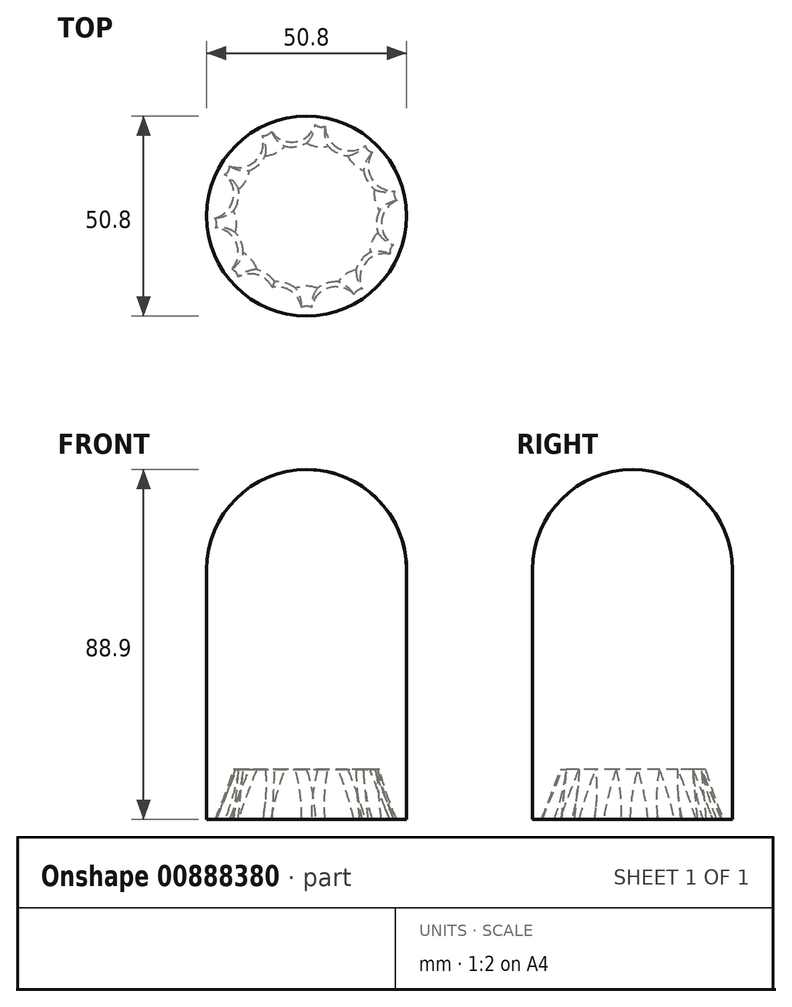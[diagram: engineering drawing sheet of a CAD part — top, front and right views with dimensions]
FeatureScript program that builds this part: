
annotation { "Feature Type Name" : "Feature", "Feature Type Description" : "" }
export const myFeature = defineFeature(function(context is Context, id is Id, definition is map)
    precondition{}
    {
        {
            var Q0;
            Q0=qCreatedBy(makeId("Front.planeOp"),FACE);
            var sketch = newSketch(context, id + "F0", { "sketchPlane" : qUnion([Q0])});
            skLineSegment(sketch, "E0.bottom", {"start": v(-25.4, 0) * mm, "end": v(25.4, 0) * mm});
            skLineSegment(sketch, "E0.top", {"start": v(-25.4, 50.8) * mm, "end": v(25.4, 50.8) * mm});
            skLineSegment(sketch, "E0.left", {"start": v(-25.4, 0) * mm, "end": v(-25.4, 50.8) * mm});
            skLineSegment(sketch, "E0.right", {"start": v(25.4, 0) * mm, "end": v(25.4, 50.8) * mm});
            skPoint(sketch, "E0.middle", {"position": v(0, 25.4) * mm});
            skArc(sketch, "E1", {"start": v(-25.4, 50.8) * mm, "mid": v(0, 76.2) * mm, "end": v(25.4, 50.8) * mm});
            skLineSegment(sketch, "E2", {"start": v(0, 0) * mm, "end": v(0, 76.2) * mm});
            skSolve(sketch);
        }
        {
            var Q0;
            {var subQ0=sQuery(id+"F0.wireOp",EDGE,"E1");var subQ3=sQuery(id+"F0.wireOp",EDGE,"E2");var subQ5=makeQuery(id+"F0.imprint","INTERSECT",VERTEX,{"derivedFrom":[subQ0,subQ3]});Q0=makeQuery(id+"F0.imprint","IMPRINT",FACE,{"disambiguationData":[TD([[makeQuery(id+"F0.imprint","IMPRINT",EDGE,{"disambiguationData":[TD([[subQ5,1.0]])],"derivedFrom":subQ3}),1.0]])]});}
            var Q1;
            {var subQ0=sQuery(id+"F0.wireOp",EDGE,"E0.left");Q1=makeQuery(id+"F0.imprint","IMPRINT",FACE,{"disambiguationData":[TD([[makeQuery(id+"F0.imprint","IMPRINT",EDGE,{"derivedFrom":subQ0}),-1.0]])]});}
            var Q2;
            Q2=sQuery(id+"F0.wireOp",EDGE,"E2");
            revolve(context, id + "F1", {"surfaceOperationType" : NewSurfaceOperationType.NEW, "entities" : qUnion([Q0, Q1]), "axis" : qUnion([Q2]), "revolveType" : RevolveType.FULL});
        }
        {
            var Q0;
            Q0=makeQuery(id+"F1.opRevolve","SWEPT_FACE",FACE,{"disambiguationData":[OSD([sQuery(id+"F0.wireOp",EDGE,"E0.bottom")])]});
            var sketch = newSketch(context, id + "F2", { "sketchPlane" : qUnion([Q0])});
            skCircle(sketch, "E3", {"center": v(0, 25.4) * mm, "radius": 7.57 * mm});
            skCircle(sketch, "E4", {"center": v(-7.49, 24.27) * mm, "radius": 7.57 * mm});
            skCircle(sketch, "E5", {"center": v(-14.3, 20.99) * mm, "radius": 7.57 * mm});
            skCircle(sketch, "E6", {"center": v(-19.86, 15.84) * mm, "radius": 7.57 * mm});
            skCircle(sketch, "E7", {"center": v(-23.64, 9.28) * mm, "radius": 7.57 * mm});
            skCircle(sketch, "E8", {"center": v(-25.33, 1.9) * mm, "radius": 7.57 * mm});
            skCircle(sketch, "E9", {"center": v(-24.76, -5.65) * mm, "radius": 7.57 * mm});
            skCircle(sketch, "E10", {"center": v(-22, -12.7) * mm, "radius": 7.57 * mm});
            skCircle(sketch, "E11", {"center": v(-17.28, -18.62) * mm, "radius": 7.57 * mm});
            skCircle(sketch, "E12", {"center": v(-11.02, -22.88) * mm, "radius": 7.57 * mm});
            skCircle(sketch, "E13", {"center": v(-3.79, -25.12) * mm, "radius": 7.57 * mm});
            skCircle(sketch, "E14", {"center": v(3.79, -25.12) * mm, "radius": 7.57 * mm});
            skCircle(sketch, "E15", {"center": v(11.02, -22.88) * mm, "radius": 7.57 * mm});
            skCircle(sketch, "E16", {"center": v(17.28, -18.62) * mm, "radius": 7.57 * mm});
            skCircle(sketch, "E17", {"center": v(22, -12.7) * mm, "radius": 7.57 * mm});
            skCircle(sketch, "E18", {"center": v(24.76, -5.65) * mm, "radius": 7.57 * mm});
            skCircle(sketch, "E19", {"center": v(25.33, 1.9) * mm, "radius": 7.57 * mm});
            skCircle(sketch, "E20", {"center": v(23.64, 9.28) * mm, "radius": 7.57 * mm});
            skCircle(sketch, "E21", {"center": v(19.86, 15.84) * mm, "radius": 7.57 * mm});
            skCircle(sketch, "E22", {"center": v(14.3, 20.99) * mm, "radius": 7.57 * mm});
            skCircle(sketch, "E23", {"center": v(7.49, 24.27) * mm, "radius": 7.57 * mm});
            skSolve(sketch);
        }
        {
            var Q0;
            Q0 = qSketchRegion(id + "F2", true);
            var Q1;
            {var subQ0=sQuery(id+"F2.wireOp",EDGE,"E12");var subQ1=sQuery(id+"F2.wireOp",EDGE,"E10");var subQ2=makeQuery(id+"F2.imprint","INTERSECT",VERTEX,{"derivedFrom":[subQ1,subQ0]});Q1=makeQuery(id+"F2.imprint","IMPRINT",FACE,{"disambiguationData":[TD([[makeQuery(id+"F2.imprint","IMPRINT",EDGE,{"disambiguationData":[TD([[subQ2,1.0]])],"derivedFrom":subQ1}),1.0]])]});}
            var Q2;
            {var subQ0=sQuery(id+"F2.wireOp",EDGE,"E12");var subQ1=sQuery(id+"F2.wireOp",EDGE,"E11");var subQ2=makeQuery(id+"F2.imprint","INTERSECT",VERTEX,{"disambiguationData":[OD(1.0)],"derivedFrom":[subQ1,subQ0]});Q2=makeQuery(id+"F2.imprint","IMPRINT",FACE,{"disambiguationData":[TD([[makeQuery(id+"F2.imprint","IMPRINT",EDGE,{"disambiguationData":[TD([[subQ2,1.0]])],"derivedFrom":subQ1}),-1.0]])]});}
            var Q3;
            {var subQ0=sQuery(id+"F2.wireOp",EDGE,"E13");var subQ1=sQuery(id+"F2.wireOp",EDGE,"E11");var subQ2=makeQuery(id+"F2.imprint","INTERSECT",VERTEX,{"derivedFrom":[subQ1,subQ0]});Q3=makeQuery(id+"F2.imprint","IMPRINT",FACE,{"disambiguationData":[TD([[makeQuery(id+"F2.imprint","IMPRINT",EDGE,{"disambiguationData":[TD([[subQ2,1.0]])],"derivedFrom":subQ1}),1.0]])]});}
            var Q4;
            {var subQ0=sQuery(id+"F2.wireOp",EDGE,"E13");var subQ1=sQuery(id+"F2.wireOp",EDGE,"E12");var subQ2=makeQuery(id+"F2.imprint","INTERSECT",VERTEX,{"disambiguationData":[OD(1.0)],"derivedFrom":[subQ1,subQ0]});Q4=makeQuery(id+"F2.imprint","IMPRINT",FACE,{"disambiguationData":[TD([[makeQuery(id+"F2.imprint","IMPRINT",EDGE,{"disambiguationData":[TD([[subQ2,1.0]])],"derivedFrom":subQ1}),-1.0]])]});}
            var Q5;
            {var subQ0=sQuery(id+"F2.wireOp",EDGE,"E15");var subQ1=sQuery(id+"F2.wireOp",EDGE,"E13");var subQ2=makeQuery(id+"F2.imprint","INTERSECT",VERTEX,{"derivedFrom":[subQ1,subQ0]});Q5=makeQuery(id+"F2.imprint","IMPRINT",FACE,{"disambiguationData":[TD([[makeQuery(id+"F2.imprint","IMPRINT",EDGE,{"disambiguationData":[TD([[subQ2,-1.0]])],"derivedFrom":subQ1}),-1.0]])]});}
            var Q6;
            {var subQ0=sQuery(id+"F2.wireOp",EDGE,"E14");var subQ1=sQuery(id+"F2.wireOp",EDGE,"E12");var subQ2=makeQuery(id+"F2.imprint","INTERSECT",VERTEX,{"derivedFrom":[subQ1,subQ0]});Q6=makeQuery(id+"F2.imprint","IMPRINT",FACE,{"disambiguationData":[TD([[makeQuery(id+"F2.imprint","IMPRINT",EDGE,{"disambiguationData":[TD([[subQ2,1.0]])],"derivedFrom":subQ1}),1.0]])]});}
            var Q7;
            {var subQ0=sQuery(id+"F2.wireOp",EDGE,"E15");var subQ1=sQuery(id+"F2.wireOp",EDGE,"E13");var subQ2=makeQuery(id+"F2.imprint","INTERSECT",VERTEX,{"derivedFrom":[subQ1,subQ0]});Q7=makeQuery(id+"F2.imprint","IMPRINT",FACE,{"disambiguationData":[TD([[makeQuery(id+"F2.imprint","IMPRINT",EDGE,{"disambiguationData":[TD([[subQ2,1.0]])],"derivedFrom":subQ1}),1.0]])]});}
            var Q8;
            {var subQ0=sQuery(id+"F2.wireOp",EDGE,"E16");var subQ1=sQuery(id+"F2.wireOp",EDGE,"E14");var subQ2=makeQuery(id+"F2.imprint","INTERSECT",VERTEX,{"derivedFrom":[subQ1,subQ0]});Q8=makeQuery(id+"F2.imprint","IMPRINT",FACE,{"disambiguationData":[TD([[makeQuery(id+"F2.imprint","IMPRINT",EDGE,{"disambiguationData":[TD([[subQ2,-1.0]])],"derivedFrom":subQ1}),-1.0]])]});}
            var Q9;
            {var subQ0=sQuery(id+"F2.wireOp",EDGE,"E17");var subQ1=sQuery(id+"F2.wireOp",EDGE,"E15");var subQ2=makeQuery(id+"F2.imprint","INTERSECT",VERTEX,{"derivedFrom":[subQ1,subQ0]});Q9=makeQuery(id+"F2.imprint","IMPRINT",FACE,{"disambiguationData":[TD([[makeQuery(id+"F2.imprint","IMPRINT",EDGE,{"disambiguationData":[TD([[subQ2,-1.0]])],"derivedFrom":subQ1}),-1.0]])]});}
            var Q10;
            {var subQ0=sQuery(id+"F2.wireOp",EDGE,"E18");var subQ1=sQuery(id+"F2.wireOp",EDGE,"E16");var subQ2=makeQuery(id+"F2.imprint","INTERSECT",VERTEX,{"derivedFrom":[subQ1,subQ0]});Q10=makeQuery(id+"F2.imprint","IMPRINT",FACE,{"disambiguationData":[TD([[makeQuery(id+"F2.imprint","IMPRINT",EDGE,{"disambiguationData":[TD([[subQ2,-1.0]])],"derivedFrom":subQ1}),-1.0]])]});}
            var Q11;
            {var subQ0=sQuery(id+"F2.wireOp",EDGE,"E17");var subQ1=sQuery(id+"F2.wireOp",EDGE,"E15");var subQ2=makeQuery(id+"F2.imprint","INTERSECT",VERTEX,{"derivedFrom":[subQ1,subQ0]});Q11=makeQuery(id+"F2.imprint","IMPRINT",FACE,{"disambiguationData":[TD([[makeQuery(id+"F2.imprint","IMPRINT",EDGE,{"disambiguationData":[TD([[subQ2,1.0]])],"derivedFrom":subQ1}),1.0]])]});}
            var Q12;
            {var subQ0=sQuery(id+"F2.wireOp",EDGE,"E16");var subQ1=sQuery(id+"F2.wireOp",EDGE,"E14");var subQ2=makeQuery(id+"F2.imprint","INTERSECT",VERTEX,{"derivedFrom":[subQ1,subQ0]});Q12=makeQuery(id+"F2.imprint","IMPRINT",FACE,{"disambiguationData":[TD([[makeQuery(id+"F2.imprint","IMPRINT",EDGE,{"disambiguationData":[TD([[subQ2,1.0]])],"derivedFrom":subQ1}),1.0]])]});}
            var Q13;
            {var subQ0=sQuery(id+"F2.wireOp",EDGE,"E20");var subQ1=sQuery(id+"F2.wireOp",EDGE,"E18");var subQ2=makeQuery(id+"F2.imprint","INTERSECT",VERTEX,{"derivedFrom":[subQ1,subQ0]});Q13=makeQuery(id+"F2.imprint","IMPRINT",FACE,{"disambiguationData":[TD([[makeQuery(id+"F2.imprint","IMPRINT",EDGE,{"disambiguationData":[TD([[subQ2,-1.0]])],"derivedFrom":subQ1}),-1.0]])]});}
            var Q14;
            {var subQ0=sQuery(id+"F2.wireOp",EDGE,"E18");var subQ1=sQuery(id+"F2.wireOp",EDGE,"E16");var subQ2=makeQuery(id+"F2.imprint","INTERSECT",VERTEX,{"derivedFrom":[subQ1,subQ0]});Q14=makeQuery(id+"F2.imprint","IMPRINT",FACE,{"disambiguationData":[TD([[makeQuery(id+"F2.imprint","IMPRINT",EDGE,{"disambiguationData":[TD([[subQ2,1.0]])],"derivedFrom":subQ1}),1.0]])]});}
            var Q15;
            {var subQ0=sQuery(id+"F2.wireOp",EDGE,"E19");var subQ1=sQuery(id+"F2.wireOp",EDGE,"E17");var subQ2=makeQuery(id+"F2.imprint","INTERSECT",VERTEX,{"derivedFrom":[subQ1,subQ0]});Q15=makeQuery(id+"F2.imprint","IMPRINT",FACE,{"disambiguationData":[TD([[makeQuery(id+"F2.imprint","IMPRINT",EDGE,{"disambiguationData":[TD([[subQ2,1.0]])],"derivedFrom":subQ1}),1.0]])]});}
            var Q16;
            {var subQ0=sQuery(id+"F2.wireOp",EDGE,"E19");var subQ1=sQuery(id+"F2.wireOp",EDGE,"E17");var subQ2=makeQuery(id+"F2.imprint","INTERSECT",VERTEX,{"derivedFrom":[subQ1,subQ0]});Q16=makeQuery(id+"F2.imprint","IMPRINT",FACE,{"disambiguationData":[TD([[makeQuery(id+"F2.imprint","IMPRINT",EDGE,{"disambiguationData":[TD([[subQ2,-1.0]])],"derivedFrom":subQ1}),-1.0]])]});}
            var Q17;
            {var subQ0=sQuery(id+"F2.wireOp",EDGE,"E20");var subQ1=sQuery(id+"F2.wireOp",EDGE,"E18");var subQ2=makeQuery(id+"F2.imprint","INTERSECT",VERTEX,{"derivedFrom":[subQ1,subQ0]});Q17=makeQuery(id+"F2.imprint","IMPRINT",FACE,{"disambiguationData":[TD([[makeQuery(id+"F2.imprint","IMPRINT",EDGE,{"disambiguationData":[TD([[subQ2,1.0]])],"derivedFrom":subQ1}),1.0]])]});}
            var Q18;
            {var subQ0=sQuery(id+"F2.wireOp",EDGE,"E21");var subQ1=sQuery(id+"F2.wireOp",EDGE,"E19");var subQ2=makeQuery(id+"F2.imprint","INTERSECT",VERTEX,{"derivedFrom":[subQ1,subQ0]});Q18=makeQuery(id+"F2.imprint","IMPRINT",FACE,{"disambiguationData":[TD([[makeQuery(id+"F2.imprint","IMPRINT",EDGE,{"disambiguationData":[TD([[subQ2,-1.0]])],"derivedFrom":subQ1}),-1.0]])]});}
            var Q19;
            {var subQ0=sQuery(id+"F2.wireOp",EDGE,"E22");var subQ1=sQuery(id+"F2.wireOp",EDGE,"E20");var subQ2=makeQuery(id+"F2.imprint","INTERSECT",VERTEX,{"derivedFrom":[subQ1,subQ0]});Q19=makeQuery(id+"F2.imprint","IMPRINT",FACE,{"disambiguationData":[TD([[makeQuery(id+"F2.imprint","IMPRINT",EDGE,{"disambiguationData":[TD([[subQ2,-1.0]])],"derivedFrom":subQ1}),-1.0]])]});}
            var Q20;
            {var subQ0=sQuery(id+"F2.wireOp",EDGE,"E21");var subQ1=sQuery(id+"F2.wireOp",EDGE,"E19");var subQ2=makeQuery(id+"F2.imprint","INTERSECT",VERTEX,{"derivedFrom":[subQ1,subQ0]});Q20=makeQuery(id+"F2.imprint","IMPRINT",FACE,{"disambiguationData":[TD([[makeQuery(id+"F2.imprint","IMPRINT",EDGE,{"disambiguationData":[TD([[subQ2,1.0]])],"derivedFrom":subQ1}),1.0]])]});}
            var Q21;
            {var subQ0=sQuery(id+"F2.wireOp",EDGE,"E22");var subQ1=sQuery(id+"F2.wireOp",EDGE,"E20");var subQ2=makeQuery(id+"F2.imprint","INTERSECT",VERTEX,{"derivedFrom":[subQ1,subQ0]});Q21=makeQuery(id+"F2.imprint","IMPRINT",FACE,{"disambiguationData":[TD([[makeQuery(id+"F2.imprint","IMPRINT",EDGE,{"disambiguationData":[TD([[subQ2,-1.0]])],"derivedFrom":subQ1}),1.0]])]});}
            var Q22;
            {var subQ0=sQuery(id+"F2.wireOp",EDGE,"E22");var subQ1=sQuery(id+"F2.wireOp",EDGE,"E20");var subQ2=makeQuery(id+"F2.imprint","INTERSECT",VERTEX,{"derivedFrom":[subQ1,subQ0]});Q22=makeQuery(id+"F2.imprint","IMPRINT",FACE,{"disambiguationData":[TD([[makeQuery(id+"F2.imprint","IMPRINT",EDGE,{"disambiguationData":[TD([[subQ2,1.0]])],"derivedFrom":subQ1}),1.0]])]});}
            var Q23;
            {var subQ0=sQuery(id+"F2.wireOp",EDGE,"E23");var subQ1=sQuery(id+"F2.wireOp",EDGE,"E21");var subQ2=makeQuery(id+"F2.imprint","INTERSECT",VERTEX,{"derivedFrom":[subQ1,subQ0]});Q23=makeQuery(id+"F2.imprint","IMPRINT",FACE,{"disambiguationData":[TD([[makeQuery(id+"F2.imprint","IMPRINT",EDGE,{"disambiguationData":[TD([[subQ2,-1.0]])],"derivedFrom":subQ1}),-1.0]])]});}
            var Q24;
            {var subQ0=sQuery(id+"F2.wireOp",EDGE,"E23");var subQ1=sQuery(id+"F2.wireOp",EDGE,"E21");var subQ2=makeQuery(id+"F2.imprint","INTERSECT",VERTEX,{"derivedFrom":[subQ1,subQ0]});Q24=makeQuery(id+"F2.imprint","IMPRINT",FACE,{"disambiguationData":[TD([[makeQuery(id+"F2.imprint","IMPRINT",EDGE,{"disambiguationData":[TD([[subQ2,1.0]])],"derivedFrom":subQ1}),1.0]])]});}
            var Q25;
            {var subQ0=sQuery(id+"F2.wireOp",EDGE,"E23");var subQ1=sQuery(id+"F2.wireOp",EDGE,"E3");var subQ2=makeQuery(id+"F2.imprint","INTERSECT",VERTEX,{"disambiguationData":[OD(1.0)],"derivedFrom":[subQ1,subQ0]});Q25=makeQuery(id+"F2.imprint","IMPRINT",FACE,{"disambiguationData":[TD([[makeQuery(id+"F2.imprint","IMPRINT",EDGE,{"disambiguationData":[TD([[subQ2,-1.0]])],"derivedFrom":subQ1}),-1.0]])]});}
            var Q26;
            {var subQ0=sQuery(id+"F2.wireOp",EDGE,"E4");var subQ1=sQuery(id+"F2.wireOp",EDGE,"E3");var subQ2=makeQuery(id+"F2.imprint","INTERSECT",VERTEX,{"disambiguationData":[OD(1.0)],"derivedFrom":[subQ1,subQ0]});Q26=makeQuery(id+"F2.imprint","IMPRINT",FACE,{"disambiguationData":[TD([[makeQuery(id+"F2.imprint","IMPRINT",EDGE,{"disambiguationData":[TD([[subQ2,-1.0]])],"derivedFrom":subQ1}),1.0]])]});}
            var Q27;
            {var subQ0=sQuery(id+"F2.wireOp",EDGE,"E22");var subQ1=sQuery(id+"F2.wireOp",EDGE,"E3");var subQ2=makeQuery(id+"F2.imprint","INTERSECT",VERTEX,{"derivedFrom":[subQ1,subQ0]});Q27=makeQuery(id+"F2.imprint","IMPRINT",FACE,{"disambiguationData":[TD([[makeQuery(id+"F2.imprint","IMPRINT",EDGE,{"disambiguationData":[TD([[subQ2,-1.0]])],"derivedFrom":subQ1}),1.0]])]});}
            var Q28;
            {var subQ0=sQuery(id+"F2.wireOp",EDGE,"E23");var subQ1=sQuery(id+"F2.wireOp",EDGE,"E4");var subQ2=makeQuery(id+"F2.imprint","INTERSECT",VERTEX,{"derivedFrom":[subQ1,subQ0]});Q28=makeQuery(id+"F2.imprint","IMPRINT",FACE,{"disambiguationData":[TD([[makeQuery(id+"F2.imprint","IMPRINT",EDGE,{"disambiguationData":[TD([[subQ2,-1.0]])],"derivedFrom":subQ1}),1.0]])]});}
            var Q29;
            {var subQ0=sQuery(id+"F2.wireOp",EDGE,"E5");var subQ1=sQuery(id+"F2.wireOp",EDGE,"E3");var subQ2=makeQuery(id+"F2.imprint","INTERSECT",VERTEX,{"derivedFrom":[subQ1,subQ0]});Q29=makeQuery(id+"F2.imprint","IMPRINT",FACE,{"disambiguationData":[TD([[makeQuery(id+"F2.imprint","IMPRINT",EDGE,{"disambiguationData":[TD([[subQ2,-1.0]])],"derivedFrom":subQ1}),-1.0]])]});}
            var Q30;
            {var subQ0=sQuery(id+"F2.wireOp",EDGE,"E5");var subQ1=sQuery(id+"F2.wireOp",EDGE,"E3");var subQ2=makeQuery(id+"F2.imprint","INTERSECT",VERTEX,{"derivedFrom":[subQ1,subQ0]});Q30=makeQuery(id+"F2.imprint","IMPRINT",FACE,{"disambiguationData":[TD([[makeQuery(id+"F2.imprint","IMPRINT",EDGE,{"disambiguationData":[TD([[subQ2,1.0]])],"derivedFrom":subQ1}),1.0]])]});}
            var Q31;
            {var subQ0=sQuery(id+"F2.wireOp",EDGE,"E6");var subQ1=sQuery(id+"F2.wireOp",EDGE,"E4");var subQ2=makeQuery(id+"F2.imprint","INTERSECT",VERTEX,{"derivedFrom":[subQ1,subQ0]});Q31=makeQuery(id+"F2.imprint","IMPRINT",FACE,{"disambiguationData":[TD([[makeQuery(id+"F2.imprint","IMPRINT",EDGE,{"disambiguationData":[TD([[subQ2,-1.0]])],"derivedFrom":subQ1}),-1.0]])]});}
            var Q32;
            {var subQ0=sQuery(id+"F2.wireOp",EDGE,"E7");var subQ1=sQuery(id+"F2.wireOp",EDGE,"E5");var subQ2=makeQuery(id+"F2.imprint","INTERSECT",VERTEX,{"derivedFrom":[subQ1,subQ0]});Q32=makeQuery(id+"F2.imprint","IMPRINT",FACE,{"disambiguationData":[TD([[makeQuery(id+"F2.imprint","IMPRINT",EDGE,{"disambiguationData":[TD([[subQ2,-1.0]])],"derivedFrom":subQ1}),-1.0]])]});}
            var Q33;
            {var subQ0=sQuery(id+"F2.wireOp",EDGE,"E6");var subQ1=sQuery(id+"F2.wireOp",EDGE,"E4");var subQ2=makeQuery(id+"F2.imprint","INTERSECT",VERTEX,{"derivedFrom":[subQ1,subQ0]});Q33=makeQuery(id+"F2.imprint","IMPRINT",FACE,{"disambiguationData":[TD([[makeQuery(id+"F2.imprint","IMPRINT",EDGE,{"disambiguationData":[TD([[subQ2,1.0]])],"derivedFrom":subQ1}),1.0]])]});}
            var Q34;
            {var subQ0=sQuery(id+"F2.wireOp",EDGE,"E7");var subQ1=sQuery(id+"F2.wireOp",EDGE,"E5");var subQ2=makeQuery(id+"F2.imprint","INTERSECT",VERTEX,{"derivedFrom":[subQ1,subQ0]});Q34=makeQuery(id+"F2.imprint","IMPRINT",FACE,{"disambiguationData":[TD([[makeQuery(id+"F2.imprint","IMPRINT",EDGE,{"disambiguationData":[TD([[subQ2,1.0]])],"derivedFrom":subQ1}),1.0]])]});}
            var Q35;
            {var subQ0=sQuery(id+"F2.wireOp",EDGE,"E8");var subQ1=sQuery(id+"F2.wireOp",EDGE,"E6");var subQ2=makeQuery(id+"F2.imprint","INTERSECT",VERTEX,{"derivedFrom":[subQ1,subQ0]});Q35=makeQuery(id+"F2.imprint","IMPRINT",FACE,{"disambiguationData":[TD([[makeQuery(id+"F2.imprint","IMPRINT",EDGE,{"disambiguationData":[TD([[subQ2,-1.0]])],"derivedFrom":subQ1}),-1.0]])]});}
            var Q36;
            {var subQ0=sQuery(id+"F2.wireOp",EDGE,"E10");var subQ1=sQuery(id+"F2.wireOp",EDGE,"E8");var subQ2=makeQuery(id+"F2.imprint","INTERSECT",VERTEX,{"derivedFrom":[subQ1,subQ0]});Q36=makeQuery(id+"F2.imprint","IMPRINT",FACE,{"disambiguationData":[TD([[makeQuery(id+"F2.imprint","IMPRINT",EDGE,{"disambiguationData":[TD([[subQ2,-1.0]])],"derivedFrom":subQ1}),-1.0]])]});}
            var Q37;
            {var subQ0=sQuery(id+"F2.wireOp",EDGE,"E9");var subQ1=sQuery(id+"F2.wireOp",EDGE,"E7");var subQ2=makeQuery(id+"F2.imprint","INTERSECT",VERTEX,{"derivedFrom":[subQ1,subQ0]});Q37=makeQuery(id+"F2.imprint","IMPRINT",FACE,{"disambiguationData":[TD([[makeQuery(id+"F2.imprint","IMPRINT",EDGE,{"disambiguationData":[TD([[subQ2,-1.0]])],"derivedFrom":subQ1}),-1.0]])]});}
            var Q38;
            {var subQ0=sQuery(id+"F2.wireOp",EDGE,"E8");var subQ1=sQuery(id+"F2.wireOp",EDGE,"E6");var subQ2=makeQuery(id+"F2.imprint","INTERSECT",VERTEX,{"derivedFrom":[subQ1,subQ0]});Q38=makeQuery(id+"F2.imprint","IMPRINT",FACE,{"disambiguationData":[TD([[makeQuery(id+"F2.imprint","IMPRINT",EDGE,{"disambiguationData":[TD([[subQ2,1.0]])],"derivedFrom":subQ1}),1.0]])]});}
            var Q39;
            {var subQ0=sQuery(id+"F2.wireOp",EDGE,"E9");var subQ1=sQuery(id+"F2.wireOp",EDGE,"E7");var subQ2=makeQuery(id+"F2.imprint","INTERSECT",VERTEX,{"derivedFrom":[subQ1,subQ0]});Q39=makeQuery(id+"F2.imprint","IMPRINT",FACE,{"disambiguationData":[TD([[makeQuery(id+"F2.imprint","IMPRINT",EDGE,{"disambiguationData":[TD([[subQ2,1.0]])],"derivedFrom":subQ1}),1.0]])]});}
            var Q40;
            {var subQ0=sQuery(id+"F2.wireOp",EDGE,"E11");var subQ1=sQuery(id+"F2.wireOp",EDGE,"E9");var subQ2=makeQuery(id+"F2.imprint","INTERSECT",VERTEX,{"derivedFrom":[subQ1,subQ0]});Q40=makeQuery(id+"F2.imprint","IMPRINT",FACE,{"disambiguationData":[TD([[makeQuery(id+"F2.imprint","IMPRINT",EDGE,{"disambiguationData":[TD([[subQ2,-1.0]])],"derivedFrom":subQ1}),-1.0]])]});}
            var Q41;
            {var subQ0=sQuery(id+"F2.wireOp",EDGE,"E11");var subQ1=sQuery(id+"F2.wireOp",EDGE,"E10");var subQ2=makeQuery(id+"F2.imprint","INTERSECT",VERTEX,{"disambiguationData":[OD(1.0)],"derivedFrom":[subQ1,subQ0]});Q41=makeQuery(id+"F2.imprint","IMPRINT",FACE,{"disambiguationData":[TD([[makeQuery(id+"F2.imprint","IMPRINT",EDGE,{"disambiguationData":[TD([[subQ2,1.0]])],"derivedFrom":subQ1}),-1.0]])]});}
            var Q42;
            {var subQ0=sQuery(id+"F2.wireOp",EDGE,"E11");var subQ1=sQuery(id+"F2.wireOp",EDGE,"E9");var subQ2=makeQuery(id+"F2.imprint","INTERSECT",VERTEX,{"derivedFrom":[subQ1,subQ0]});Q42=makeQuery(id+"F2.imprint","IMPRINT",FACE,{"disambiguationData":[TD([[makeQuery(id+"F2.imprint","IMPRINT",EDGE,{"disambiguationData":[TD([[subQ2,1.0]])],"derivedFrom":subQ1}),1.0]])]});}
            var Q43;
            {var subQ0=sQuery(id+"F2.wireOp",EDGE,"E10");var subQ1=sQuery(id+"F2.wireOp",EDGE,"E8");var subQ2=makeQuery(id+"F2.imprint","INTERSECT",VERTEX,{"derivedFrom":[subQ1,subQ0]});Q43=makeQuery(id+"F2.imprint","IMPRINT",FACE,{"disambiguationData":[TD([[makeQuery(id+"F2.imprint","IMPRINT",EDGE,{"disambiguationData":[TD([[subQ2,1.0]])],"derivedFrom":subQ1}),1.0]])]});}
            extrude(context, id + "F3", {"entities" : qUnion([Q0, Q1, Q2, Q3, Q4, Q5, Q6, Q7, Q8, Q9, Q10, Q11, Q12, Q13, Q14, Q15, Q16, Q17, Q18, Q19, Q20, Q21, Q22, Q23, Q24, Q25, Q26, Q27, Q28, Q29, Q30, Q31, Q32, Q33, Q34, Q35, Q36, Q37, Q38, Q39, Q40, Q41, Q42, Q43]), "operationType" : NewBodyOperationType.ADD, "depth" : 12.7 * mm, "offsetDistance" : 25.4 * mm});
        }
        {
            var Q0;
            Q0=makeQuery(id+"F3.opExtrude","CAP_FACE",FACE,{"disambiguationData":[OSD([sQuery(id+"F2.wireOp",EDGE,"E3"),sQuery(id+"F2.wireOp",EDGE,"E4"),sQuery(id+"F2.wireOp",EDGE,"E5"),sQuery(id+"F2.wireOp",EDGE,"E6"),sQuery(id+"F2.wireOp",EDGE,"E7"),sQuery(id+"F2.wireOp",EDGE,"E8"),sQuery(id+"F2.wireOp",EDGE,"E9"),sQuery(id+"F2.wireOp",EDGE,"E10"),sQuery(id+"F2.wireOp",EDGE,"E11"),sQuery(id+"F2.wireOp",EDGE,"E12"),sQuery(id+"F2.wireOp",EDGE,"E13"),sQuery(id+"F2.wireOp",EDGE,"E14"),sQuery(id+"F2.wireOp",EDGE,"E15"),sQuery(id+"F2.wireOp",EDGE,"E16"),sQuery(id+"F2.wireOp",EDGE,"E17"),sQuery(id+"F2.wireOp",EDGE,"E18"),sQuery(id+"F2.wireOp",EDGE,"E19"),sQuery(id+"F2.wireOp",EDGE,"E20"),sQuery(id+"F2.wireOp",EDGE,"E21"),sQuery(id+"F2.wireOp",EDGE,"E22"),sQuery(id+"F2.wireOp",EDGE,"E23")])],"isStart":true});
            var sketch = newSketch(context, id + "F4", { "sketchPlane" : qUnion([Q0])});
            skLineSegment(sketch, "E24.bottom", {"start": v(-39.67, 38.84) * mm, "end": v(43.63, 38.84) * mm});
            skLineSegment(sketch, "E24.top", {"start": v(-39.67, -41.46) * mm, "end": v(43.63, -41.46) * mm});
            skLineSegment(sketch, "E24.left", {"start": v(-39.67, 38.84) * mm, "end": v(-39.67, -41.46) * mm});
            skLineSegment(sketch, "E24.right", {"start": v(43.63, 38.84) * mm, "end": v(43.63, -41.46) * mm});
            skCircle(sketch, "E25", {"center": v(0, 0) * mm, "radius": 25.4 * mm});
            skSolve(sketch);
        }
        {
            var Q0;
            Q0 = qSketchRegion(id + "F4", true);
            extrude(context, id + "F5", {"entities" : qUnion([Q0]), "operationType" : NewBodyOperationType.REMOVE, "oppositeDirection" : true, "depth" : 25.4 * mm, "offsetDistance" : 25.4 * mm});
        }
        {
            var Q0;
            {var subQ0=sQuery(id+"F2.wireOp",EDGE,"E22");Q0=makeQuery(id+"F3.opExtrude","CAP_EDGE",EDGE,{"disambiguationData":[OSD([subQ0]),TDD([makeQuery(id+"F2.imprint","IMPRINT",EDGE,{"disambiguationData":[TD([[makeQuery(id+"F2.imprint","INTERSECT",VERTEX,{"disambiguationData":[OD(1.0)],"derivedFrom":[sQuery(id+"F2.wireOp",EDGE,"E21"),subQ0]}),1.0]])],"derivedFrom":subQ0})])],"isStart":false});}
            var Q1;
            {var subQ0=sQuery(id+"F2.wireOp",EDGE,"E3");Q1=makeQuery(id+"F3.opExtrude","CAP_EDGE",EDGE,{"disambiguationData":[OSD([subQ0]),TDD([makeQuery(id+"F2.imprint","IMPRINT",EDGE,{"disambiguationData":[TD([[makeQuery(id+"F2.imprint","INTERSECT",VERTEX,{"disambiguationData":[OD(1.0)],"derivedFrom":[subQ0,sQuery(id+"F2.wireOp",EDGE,"E4")]}),-1.0]])],"derivedFrom":subQ0})])],"isStart":false});}
            var Q2;
            {var subQ0=sQuery(id+"F2.wireOp",EDGE,"E20");Q2=makeQuery(id+"F3.opExtrude","CAP_EDGE",EDGE,{"disambiguationData":[OSD([subQ0]),TDD([makeQuery(id+"F2.imprint","IMPRINT",EDGE,{"disambiguationData":[TD([[makeQuery(id+"F2.imprint","INTERSECT",VERTEX,{"disambiguationData":[OD(1.0)],"derivedFrom":[sQuery(id+"F2.wireOp",EDGE,"E19"),subQ0]}),1.0]])],"derivedFrom":subQ0})])],"isStart":false});}
            var Q3;
            {var subQ0=sQuery(id+"F2.wireOp",EDGE,"E18");Q3=makeQuery(id+"F3.opExtrude","CAP_EDGE",EDGE,{"disambiguationData":[OSD([subQ0]),TDD([makeQuery(id+"F2.imprint","IMPRINT",EDGE,{"disambiguationData":[TD([[makeQuery(id+"F2.imprint","INTERSECT",VERTEX,{"disambiguationData":[OD(1.0)],"derivedFrom":[sQuery(id+"F2.wireOp",EDGE,"E17"),subQ0]}),1.0]])],"derivedFrom":subQ0})])],"isStart":false});}
            var Q4;
            {var subQ0=sQuery(id+"F2.wireOp",EDGE,"E16");Q4=makeQuery(id+"F3.opExtrude","CAP_EDGE",EDGE,{"disambiguationData":[OSD([subQ0]),TDD([makeQuery(id+"F2.imprint","IMPRINT",EDGE,{"disambiguationData":[TD([[makeQuery(id+"F2.imprint","INTERSECT",VERTEX,{"disambiguationData":[OD(1.0)],"derivedFrom":[sQuery(id+"F2.wireOp",EDGE,"E15"),subQ0]}),1.0]])],"derivedFrom":subQ0})])],"isStart":false});}
            var Q5;
            {var subQ0=sQuery(id+"F2.wireOp",EDGE,"E14");Q5=makeQuery(id+"F3.opExtrude","CAP_EDGE",EDGE,{"disambiguationData":[OSD([subQ0]),TDD([makeQuery(id+"F2.imprint","IMPRINT",EDGE,{"disambiguationData":[TD([[makeQuery(id+"F2.imprint","INTERSECT",VERTEX,{"disambiguationData":[OD(1.0)],"derivedFrom":[sQuery(id+"F2.wireOp",EDGE,"E13"),subQ0]}),1.0]])],"derivedFrom":subQ0})])],"isStart":false});}
            var Q6;
            {var subQ0=sQuery(id+"F2.wireOp",EDGE,"E12");Q6=makeQuery(id+"F3.opExtrude","CAP_EDGE",EDGE,{"disambiguationData":[OSD([subQ0]),TDD([makeQuery(id+"F2.imprint","IMPRINT",EDGE,{"disambiguationData":[TD([[makeQuery(id+"F2.imprint","INTERSECT",VERTEX,{"disambiguationData":[OD(1.0)],"derivedFrom":[sQuery(id+"F2.wireOp",EDGE,"E11"),subQ0]}),1.0]])],"derivedFrom":subQ0})])],"isStart":false});}
            var Q7;
            {var subQ0=sQuery(id+"F2.wireOp",EDGE,"E10");Q7=makeQuery(id+"F3.opExtrude","CAP_EDGE",EDGE,{"disambiguationData":[OSD([subQ0]),TDD([makeQuery(id+"F2.imprint","IMPRINT",EDGE,{"disambiguationData":[TD([[makeQuery(id+"F2.imprint","INTERSECT",VERTEX,{"disambiguationData":[OD(1.0)],"derivedFrom":[sQuery(id+"F2.wireOp",EDGE,"E9"),subQ0]}),1.0]])],"derivedFrom":subQ0})])],"isStart":false});}
            var Q8;
            {var subQ0=sQuery(id+"F2.wireOp",EDGE,"E8");Q8=makeQuery(id+"F3.opExtrude","CAP_EDGE",EDGE,{"disambiguationData":[OSD([subQ0]),TDD([makeQuery(id+"F2.imprint","IMPRINT",EDGE,{"disambiguationData":[TD([[makeQuery(id+"F2.imprint","INTERSECT",VERTEX,{"disambiguationData":[OD(1.0)],"derivedFrom":[sQuery(id+"F2.wireOp",EDGE,"E7"),subQ0]}),1.0]])],"derivedFrom":subQ0})])],"isStart":false});}
            var Q9;
            {var subQ0=sQuery(id+"F2.wireOp",EDGE,"E6");Q9=makeQuery(id+"F3.opExtrude","CAP_EDGE",EDGE,{"disambiguationData":[OSD([subQ0]),TDD([makeQuery(id+"F2.imprint","IMPRINT",EDGE,{"disambiguationData":[TD([[makeQuery(id+"F2.imprint","INTERSECT",VERTEX,{"disambiguationData":[OD(1.0)],"derivedFrom":[sQuery(id+"F2.wireOp",EDGE,"E5"),subQ0]}),1.0]])],"derivedFrom":subQ0})])],"isStart":false});}
            chamfer(context, id + "F6", {"entities" : qUnion([Q0, Q1, Q2, Q3, Q4, Q5, Q6, Q7, Q8, Q9]), "chamferType" : ChamferType.TWO_OFFSETS, "width1" : 12.7 * mm, "oppositeDirection" : true, "width2" : 5.08 * mm, "tangentPropagation" : true});
        }
        {
            var Q0;
            {var subQ0=sQuery(id+"F2.wireOp",EDGE,"E23");Q0=makeQuery(id+"F3.opExtrude","CAP_EDGE",EDGE,{"disambiguationData":[OSD([subQ0]),TDD([makeQuery(id+"F2.imprint","IMPRINT",EDGE,{"disambiguationData":[TD([[makeQuery(id+"F2.imprint","INTERSECT",VERTEX,{"disambiguationData":[OD(1.0)],"derivedFrom":[sQuery(id+"F2.wireOp",EDGE,"E3"),subQ0]}),-1.0]])],"derivedFrom":subQ0})])],"isStart":false});}
            var Q1;
            {var subQ0=sQuery(id+"F2.wireOp",EDGE,"E21");Q1=makeQuery(id+"F3.opExtrude","CAP_EDGE",EDGE,{"disambiguationData":[OSD([subQ0]),TDD([makeQuery(id+"F2.imprint","IMPRINT",EDGE,{"disambiguationData":[TD([[makeQuery(id+"F2.imprint","INTERSECT",VERTEX,{"disambiguationData":[OD(1.0)],"derivedFrom":[sQuery(id+"F2.wireOp",EDGE,"E20"),subQ0]}),1.0]])],"derivedFrom":subQ0})])],"isStart":false});}
            var Q2;
            {var subQ0=sQuery(id+"F2.wireOp",EDGE,"E4");Q2=makeQuery(id+"F3.opExtrude","CAP_EDGE",EDGE,{"disambiguationData":[OSD([subQ0]),TDD([makeQuery(id+"F2.imprint","IMPRINT",EDGE,{"disambiguationData":[TD([[makeQuery(id+"F2.imprint","INTERSECT",VERTEX,{"disambiguationData":[OD(1.0)],"derivedFrom":[sQuery(id+"F2.wireOp",EDGE,"E3"),subQ0]}),1.0]])],"derivedFrom":subQ0})])],"isStart":false});}
            var Q3;
            {var subQ0=sQuery(id+"F2.wireOp",EDGE,"E5");Q3=makeQuery(id+"F3.opExtrude","CAP_EDGE",EDGE,{"disambiguationData":[OSD([subQ0]),TDD([makeQuery(id+"F2.imprint","IMPRINT",EDGE,{"disambiguationData":[TD([[makeQuery(id+"F2.imprint","INTERSECT",VERTEX,{"disambiguationData":[OD(1.0)],"derivedFrom":[sQuery(id+"F2.wireOp",EDGE,"E4"),subQ0]}),1.0]])],"derivedFrom":subQ0})])],"isStart":false});}
            var Q4;
            {var subQ0=sQuery(id+"F2.wireOp",EDGE,"E7");Q4=makeQuery(id+"F3.opExtrude","CAP_EDGE",EDGE,{"disambiguationData":[OSD([subQ0]),TDD([makeQuery(id+"F2.imprint","IMPRINT",EDGE,{"disambiguationData":[TD([[makeQuery(id+"F2.imprint","INTERSECT",VERTEX,{"disambiguationData":[OD(1.0)],"derivedFrom":[sQuery(id+"F2.wireOp",EDGE,"E6"),subQ0]}),1.0]])],"derivedFrom":subQ0})])],"isStart":false});}
            var Q5;
            {var subQ0=sQuery(id+"F2.wireOp",EDGE,"E9");Q5=makeQuery(id+"F3.opExtrude","CAP_EDGE",EDGE,{"disambiguationData":[OSD([subQ0]),TDD([makeQuery(id+"F2.imprint","IMPRINT",EDGE,{"disambiguationData":[TD([[makeQuery(id+"F2.imprint","INTERSECT",VERTEX,{"disambiguationData":[OD(1.0)],"derivedFrom":[sQuery(id+"F2.wireOp",EDGE,"E8"),subQ0]}),1.0]])],"derivedFrom":subQ0})])],"isStart":false});}
            var Q6;
            {var subQ0=sQuery(id+"F2.wireOp",EDGE,"E11");Q6=makeQuery(id+"F3.opExtrude","CAP_EDGE",EDGE,{"disambiguationData":[OSD([subQ0]),TDD([makeQuery(id+"F2.imprint","IMPRINT",EDGE,{"disambiguationData":[TD([[makeQuery(id+"F2.imprint","INTERSECT",VERTEX,{"disambiguationData":[OD(1.0)],"derivedFrom":[sQuery(id+"F2.wireOp",EDGE,"E10"),subQ0]}),1.0]])],"derivedFrom":subQ0})])],"isStart":false});}
            var Q7;
            {var subQ0=sQuery(id+"F2.wireOp",EDGE,"E13");Q7=makeQuery(id+"F3.opExtrude","CAP_EDGE",EDGE,{"disambiguationData":[OSD([subQ0]),TDD([makeQuery(id+"F2.imprint","IMPRINT",EDGE,{"disambiguationData":[TD([[makeQuery(id+"F2.imprint","INTERSECT",VERTEX,{"disambiguationData":[OD(1.0)],"derivedFrom":[sQuery(id+"F2.wireOp",EDGE,"E12"),subQ0]}),1.0]])],"derivedFrom":subQ0})])],"isStart":false});}
            var Q8;
            {var subQ0=sQuery(id+"F2.wireOp",EDGE,"E15");Q8=makeQuery(id+"F3.opExtrude","CAP_EDGE",EDGE,{"disambiguationData":[OSD([subQ0]),TDD([makeQuery(id+"F2.imprint","IMPRINT",EDGE,{"disambiguationData":[TD([[makeQuery(id+"F2.imprint","INTERSECT",VERTEX,{"disambiguationData":[OD(1.0)],"derivedFrom":[sQuery(id+"F2.wireOp",EDGE,"E14"),subQ0]}),1.0]])],"derivedFrom":subQ0})])],"isStart":false});}
            var Q9;
            {var subQ0=sQuery(id+"F2.wireOp",EDGE,"E17");Q9=makeQuery(id+"F3.opExtrude","CAP_EDGE",EDGE,{"disambiguationData":[OSD([subQ0]),TDD([makeQuery(id+"F2.imprint","IMPRINT",EDGE,{"disambiguationData":[TD([[makeQuery(id+"F2.imprint","INTERSECT",VERTEX,{"disambiguationData":[OD(1.0)],"derivedFrom":[sQuery(id+"F2.wireOp",EDGE,"E16"),subQ0]}),1.0]])],"derivedFrom":subQ0})])],"isStart":false});}
            var Q10;
            {var subQ0=sQuery(id+"F2.wireOp",EDGE,"E19");Q10=makeQuery(id+"F3.opExtrude","CAP_EDGE",EDGE,{"disambiguationData":[OSD([subQ0]),TDD([makeQuery(id+"F2.imprint","IMPRINT",EDGE,{"disambiguationData":[TD([[makeQuery(id+"F2.imprint","INTERSECT",VERTEX,{"disambiguationData":[OD(1.0)],"derivedFrom":[sQuery(id+"F2.wireOp",EDGE,"E18"),subQ0]}),1.0]])],"derivedFrom":subQ0})])],"isStart":false});}
            chamfer(context, id + "F7", {"entities" : qUnion([Q0, Q1, Q2, Q3, Q4, Q5, Q6, Q7, Q8, Q9, Q10]), "chamferType" : ChamferType.TWO_OFFSETS, "width1" : 12.7 * mm, "oppositeDirection" : true, "width2" : 1.27 * mm, "tangentPropagation" : true});
        }
    });
